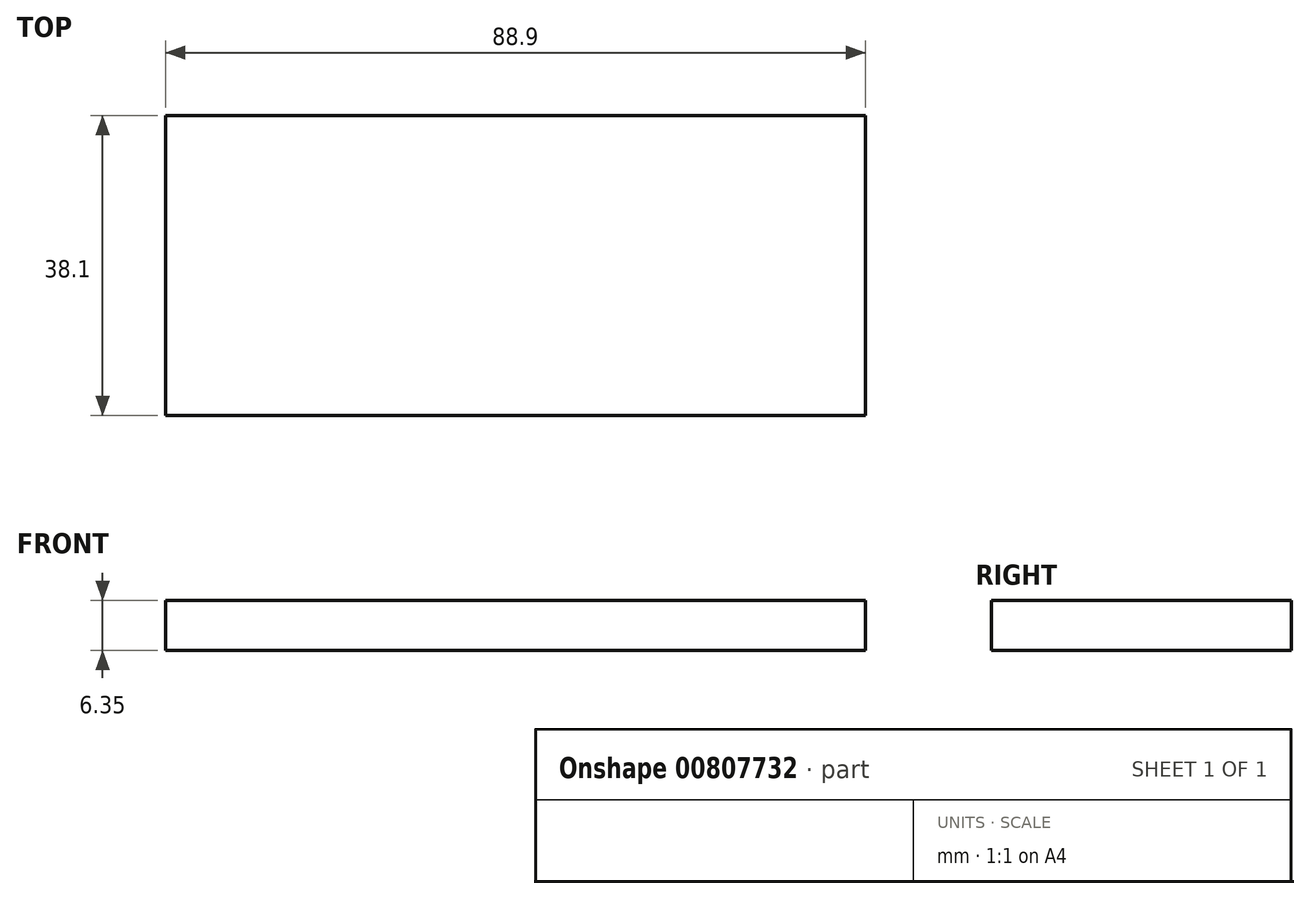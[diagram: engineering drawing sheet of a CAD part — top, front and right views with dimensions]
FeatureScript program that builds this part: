
annotation { "Feature Type Name" : "Feature", "Feature Type Description" : "" }
export const myFeature = defineFeature(function(context is Context, id is Id, definition is map)
    precondition{}
    {
        {
            var Q0;
            Q0=qCreatedBy(makeId("Top.planeOp"),FACE);
            var sketch = newSketch(context, id + "F0", { "sketchPlane" : qUnion([Q0])});
            skLineSegment(sketch, "E0", {"start": v(0, 0) * mm, "end": v(0, 38.1) * mm});
            skLineSegment(sketch, "E1", {"start": v(0, 0) * mm, "end": v(88.9, 0) * mm});
            skLineSegment(sketch, "E2", {"start": v(88.9, 0) * mm, "end": v(88.9, 38.1) * mm});
            skLineSegment(sketch, "E3", {"start": v(0, 38.1) * mm, "end": v(88.9, 38.1) * mm});
            skSolve(sketch);
        }
        {
            var Q0;
            Q0=makeQuery(id+"F0.imprint","IMPRINT",FACE,{"disambiguationData":[TD([[makeQuery(id+"F0.imprint","IMPRINT",EDGE,{"derivedFrom":sQuery(id+"F0.wireOp",EDGE,"E0")}),-1.0]])]});
            extrude(context, id + "F1", {"entities" : qUnion([Q0]), "depth" : 6.35 * mm, "offsetDistance" : 25.4 * mm});
        }
    });
